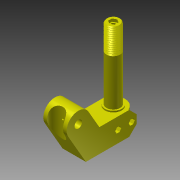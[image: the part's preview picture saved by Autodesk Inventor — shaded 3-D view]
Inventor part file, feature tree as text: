
AUTODESK INVENTOR PART (.ipt)
format: ipt  version: 2013 (Build 170138000, 138)  size: 476,160 bytes
history: native  units: mm
features: sketch x18, extrude x17, projected_geometry x3, helix x1
ambient origin geometry x8: Origin, YZ Plane, XZ Plane, XY Plane, X Axis, Y Axis, Z Axis, Center Point
bodies: Solid1 (feature_tree)
feature tree (39):
  extrude  "Extrusion1"  Depth=50.0mm
  extrude  "Extrusion2"  Depth=25.0mm
  extrude  "Extrusion13"  Depth=25.0mm TaperAngle=0.0deg
  extrude  "Extrusion12"  TaperAngle=120.0deg  [1 undecoded]
  extrude  "Extrusion14"  Depth=19.0mm TaperAngle=0.0deg
  extrude  "Extrusion15"  Depth=9.0mm
  extrude  "Extrusion16"  Depth=3.1mm
  extrude  "Extrusion17"  Depth=19.0mm TaperAngle=0.0deg
  extrude  "Extrusion18"  Depth=4.0mm TaperAngle=0.0deg
  helix  "Coil1"  [1 undecoded]
  extrude  "Extrusion19"  Depth=18.0mm
  extrude  "Extrusion20"  Depth=14.7mm
  extrude  "Extrusion21"  Depth=2.0mm
  extrude  "Extrusion22"  Depth=49.5mm TaperAngle=0.0deg
  extrude  "Extrusion23"  Depth=40.0mm
  extrude  "Extrusion24"  Depth=5.0mm
  extrude  "Extrusion25"  Depth=0.4mm TaperAngle=0.0deg
  extrude  "Extrusion26"  Depth=5.5mm TaperAngle=0.0deg
  sketch  "Sketch1"  dims[d0=8.1mm d2=50.0mm]
  sketch  "Sketch2"  dims[d3=14.0mm d4=25.0mm]
  sketch  "Sketch12"  dims[d6=25.0mm d7=25.0mm d8=0.0mm]
  sketch  "Sketch13"  dims[d9=25.0mm d10=0.0mm d40=120.0deg]
  projected_geometry  "Projected Loop1"
  sketch  "Sketch14"  dims[d56=16.2mm d58=19.0mm d59=0.0mm]
  projected_geometry  "Projected Loop2"
  sketch  "Sketch15"  dims[d60=45.0deg d61=9.0mm]
  sketch  "Sketch16"  dims[d62=19.0mm d63=0.0mm d65=3.1mm]
  sketch  "Sketch17"  dims[d67=14.5mm d68=19.0mm d69=0.0mm]
  sketch  "Sketch18"  dims[d70=6.5mm d72=4.0mm d73=0.0mm d74=5.6mm]
  sketch  "Sketch19"  dims[d75=4.0mm d76=0.0mm d77=18.0mm]
  sketch  "Sketch20"  dims[d80=1.5mm d81=0.0mm d82=14.7mm]
  sketch  "Sketch21"  dims[d85=76.5mm d86=0.0mm d87=2.0mm]
  sketch  "Sketch22"  dims[d88=2.001mm d89=10.0mm d90=300.0mm d91=0.0mm d92=90.0deg d93=90.0deg d94=0.0mm d95=0.0mm d96=49.5mm d97=0.0mm]
  sketch  "Sketch23"  dims[d98=5.0mm d99=-7.853982mm d100=40.0mm]
  sketch  "Sketch24"  dims[d102=5.0mm d103=-7.853982mm d104=5.0mm]
  sketch  "Sketch25"  dims[d106=5.0mm d107=0.0mm d115=0.4mm d116=0.0mm]
  sketch  "Sketch26"  dims[d117=13.2mm d118=5.5mm d119=0.0mm]
  sketch  "Sketch27"  dims[d120=17.0mm d122=5.5mm d123=0.0mm d125=7.2mm d126=3.0mm d127=0.0mm]
  projected_geometry  "Project Cut Edges1"
note: 2 required parameter values undecoded (feature->parameter linkage not recoverable at this tier; creation-order binding heuristic only, values carry confidence <= 0.55)
